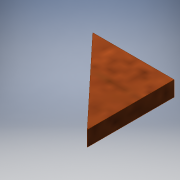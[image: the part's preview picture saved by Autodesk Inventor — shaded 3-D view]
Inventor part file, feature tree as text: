
AUTODESK INVENTOR PART (.ipt)
format: ipt  version: 2016 (Build 200138000, 138)  size: 91,648 bytes
history: native  units: mm
features: other x1, extrude x1, sketch x1
ambient origin geometry x8: Origin, YZ Plane, XZ Plane, XY Plane, X Axis, Y Axis, Z Axis, Center Point
bodies: Body1 (feature_tree)
feature tree (3):
  other  "Sólido1"
  extrude  "Extrusión1"  [1 undecoded]
  sketch  "Boceto1"  dims[d0=3.0mm d1=0.0mm]
note: 1 required parameter value undecoded (feature->parameter linkage not recoverable at this tier; creation-order binding heuristic only, values carry confidence <= 0.55)
